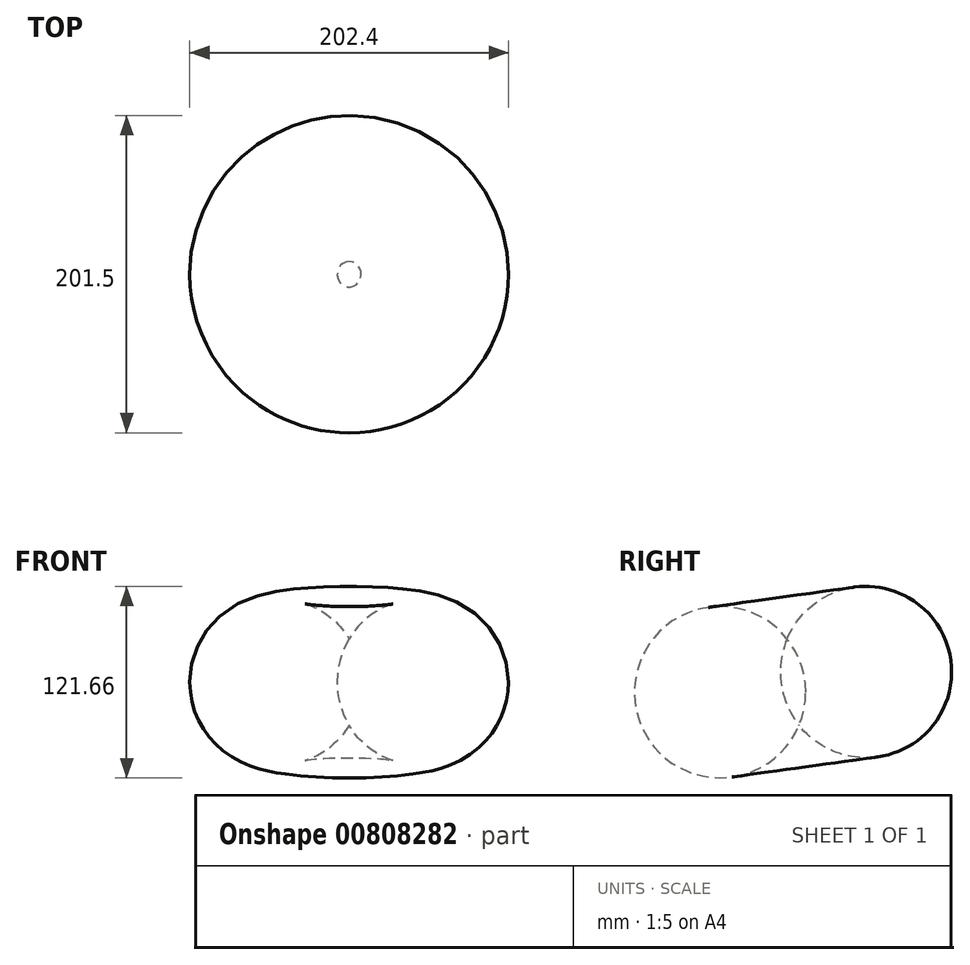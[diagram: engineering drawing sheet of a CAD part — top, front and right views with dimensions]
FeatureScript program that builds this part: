
annotation { "Feature Type Name" : "Feature", "Feature Type Description" : "" }
export const myFeature = defineFeature(function(context is Context, id is Id, definition is map)
    precondition{}
    {
        {
            var Q0;
            Q0=qCreatedBy(makeId("Right.planeOp"),FACE);
            var sketch = newSketch(context, id + "F0", { "sketchPlane" : qUnion([Q0])});
            skCircle(sketch, "E0", {"center": v(-69.17, 25.78) * mm, "radius": 54.4 * mm});
            skLineSegment(sketch, "E1", {"start": v(-29.13, 77.7) * mm, "end": v(-17.14, -8.74) * mm});
            skSolve(sketch);
        }
        {
            var Q0;
            {var subQ0=sQuery(id+"F0.wireOp",EDGE,"E1");var subQ1=sQuery(id+"F0.wireOp",EDGE,"E0");var subQ2=makeQuery(id+"F0.imprint","INTERSECT",VERTEX,{"disambiguationData":[OD(0.0)],"derivedFrom":[subQ1,subQ0]});Q0=makeQuery(id+"F0.imprint","IMPRINT",FACE,{"disambiguationData":[TD([[makeQuery(id+"F0.imprint","IMPRINT",EDGE,{"disambiguationData":[TD([[subQ2,1.0]])],"derivedFrom":subQ1}),1.0]])]});}
            var Q1;
            Q1=sQuery(id+"F0.wireOp",EDGE,"E1");
            revolve(context, id + "F1", {"surfaceOperationType" : NewSurfaceOperationType.NEW, "entities" : qUnion([Q0]), "axis" : qUnion([Q1]), "revolveType" : RevolveType.FULL});
        }
    });
